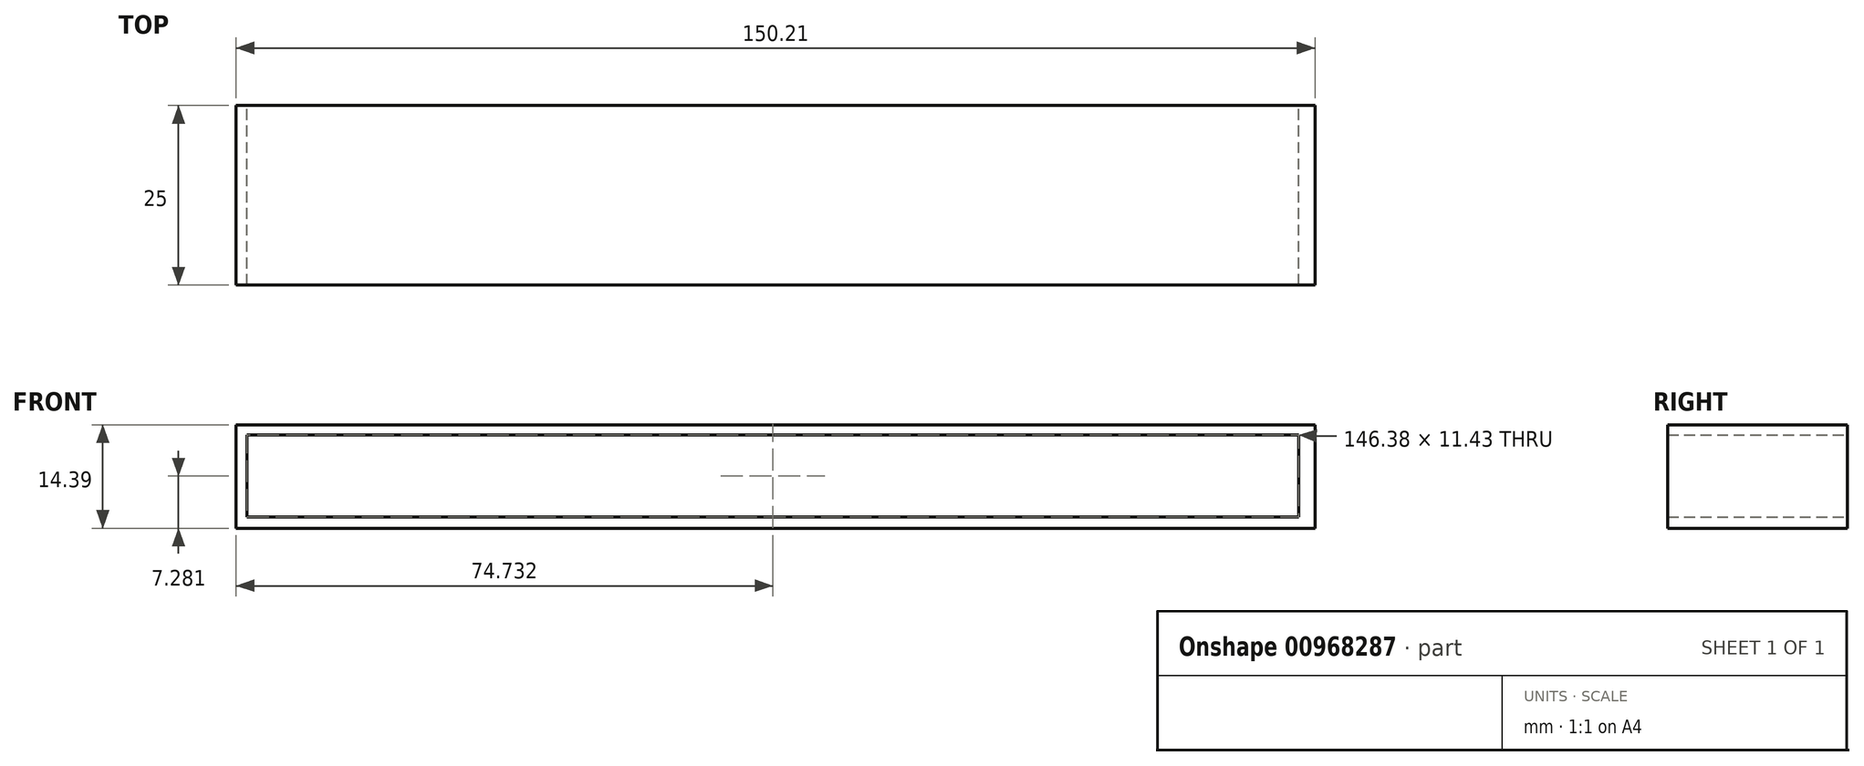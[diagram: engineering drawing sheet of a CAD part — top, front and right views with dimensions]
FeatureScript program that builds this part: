
annotation { "Feature Type Name" : "Feature", "Feature Type Description" : "" }
export const myFeature = defineFeature(function(context is Context, id is Id, definition is map)
    precondition{}
    {
        {
            var Q0;
            Q0=qCreatedBy(makeId("Front.planeOp"),FACE);
            var sketch = newSketch(context, id + "F0", { "sketchPlane" : qUnion([Q0])});
            skCircle(sketch, "E0", {"center": v(-38.74, -32.66) * mm, "radius": 22.86 * mm});
            skLineSegment(sketch, "E1.bottom", {"start": v(-38.74, -32.66) * mm, "end": v(0, -32.66) * mm});
            skLineSegment(sketch, "E1.top", {"start": v(-38.74, 0) * mm, "end": v(0, 0) * mm});
            skLineSegment(sketch, "E1.left", {"start": v(-38.74, -32.66) * mm, "end": v(-38.74, 0) * mm});
            skLineSegment(sketch, "E1.right", {"start": v(0, -32.66) * mm, "end": v(0, 0) * mm});
            skLineSegment(sketch, "E2.bottom", {"start": v(-75.2, 75.48) * mm, "end": v(75.01, 75.48) * mm});
            skLineSegment(sketch, "E2.top", {"start": v(-75.2, 11.77) * mm, "end": v(75.01, 11.77) * mm});
            skLineSegment(sketch, "E2.left", {"start": v(-75.2, 75.48) * mm, "end": v(-75.2, 11.77) * mm});
            skLineSegment(sketch, "E2.right", {"start": v(75.01, 75.48) * mm, "end": v(75.01, 11.77) * mm});
            skLineSegment(sketch, "E3", {"start": v(-75.2, 61.1) * mm, "end": v(75.01, 61.1) * mm});
            skLineSegment(sketch, "E4", {"start": v(-75.2, 52.31) * mm, "end": v(-59.32, 52.31) * mm});
            skLineSegment(sketch, "E5", {"start": v(-45.68, 52.31) * mm, "end": v(-23.45, 52.31) * mm});
            skLineSegment(sketch, "E6", {"start": v(-23.45, 52.31) * mm, "end": v(-23.45, 38.11) * mm});
            skLineSegment(sketch, "E7", {"start": v(-23.45, 38.11) * mm, "end": v(-75.2, 38.11) * mm});
            skLineSegment(sketch, "E8.bottom", {"start": v(-73.66, 74.09) * mm, "end": v(72.72, 74.09) * mm});
            skLineSegment(sketch, "E8.top", {"start": v(-73.66, 62.65) * mm, "end": v(72.72, 62.65) * mm});
            skLineSegment(sketch, "E8.left", {"start": v(-73.66, 74.09) * mm, "end": v(-73.66, 62.65) * mm});
            skLineSegment(sketch, "E8.right", {"start": v(72.72, 74.09) * mm, "end": v(72.72, 62.65) * mm});
            skSolve(sketch);
        }
        {
            var Q0;
            {var subQ1=sQuery(id+"F0.wireOp",EDGE,"E2.bottom");Q0=makeQuery(id+"F0.imprint","IMPRINT",FACE,{"disambiguationData":[TD([[makeQuery(id+"F0.imprint","IMPRINT",EDGE,{"derivedFrom":subQ1}),-1.0]])]});}
            extrude(context, id + "F1", {"entities" : qUnion([Q0]), "depth" : 25 * mm, "offsetDistance" : 25 * mm});
        }
    });
